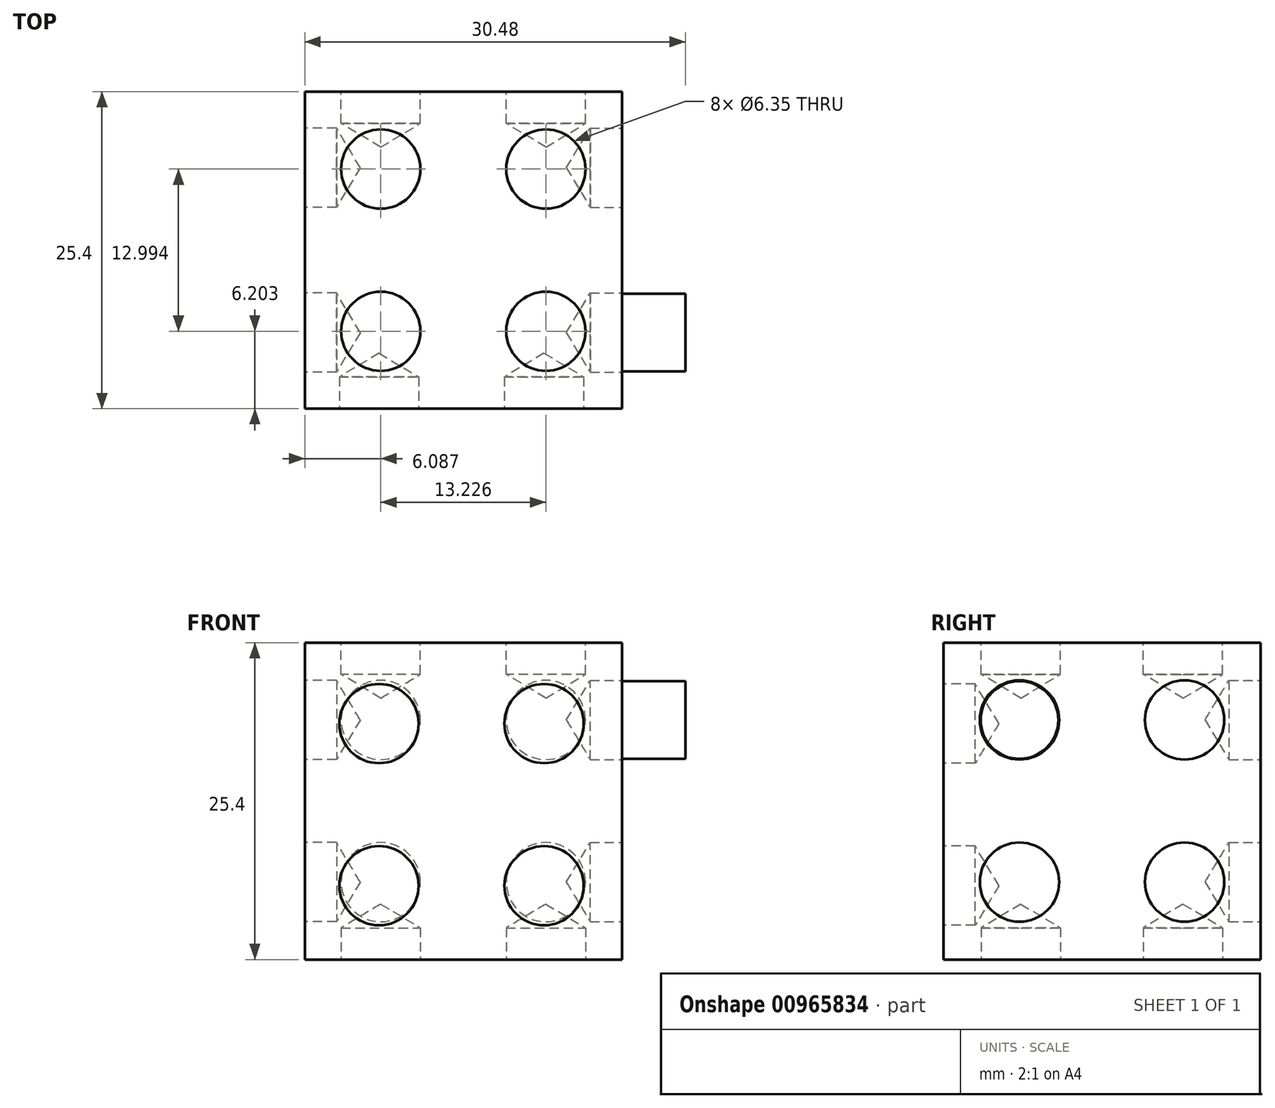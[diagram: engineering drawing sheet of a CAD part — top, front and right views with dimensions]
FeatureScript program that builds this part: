
annotation { "Feature Type Name" : "Feature", "Feature Type Description" : "" }
export const myFeature = defineFeature(function(context is Context, id is Id, definition is map)
    precondition{}
    {
        {
            var Q0;
            Q0=qCreatedBy(makeId("Front.planeOp"),FACE);
            var sketch = newSketch(context, id + "F0", { "sketchPlane" : qUnion([Q0])});
            skLineSegment(sketch, "E0.bottom", {"start": v(12.7, -12.7) * mm, "end": v(-12.7, -12.7) * mm});
            skLineSegment(sketch, "E0.top", {"start": v(12.7, 12.7) * mm, "end": v(-12.7, 12.7) * mm});
            skLineSegment(sketch, "E0.left", {"start": v(12.7, -12.7) * mm, "end": v(12.7, 12.7) * mm});
            skLineSegment(sketch, "E0.right", {"start": v(-12.7, -12.7) * mm, "end": v(-12.7, 12.7) * mm});
            skPoint(sketch, "E0.middle", {"position": v(0, 0) * mm});
            skSolve(sketch);
        }
        {
            var Q0;
            Q0 = qSketchRegion(id + "F0", true);
            extrude(context, id + "F1", {"entities" : qUnion([Q0]), "endBound" : BoundingType.SYMMETRIC, "depth" : 25.4 * mm, "offsetDistance" : 25.4 * mm});
        }
        {
            var Q0;
            Q0=makeQuery(id+"F1.opExtrude","CAP_FACE",FACE,{"disambiguationData":[OSD([sQuery(id+"F0.wireOp",EDGE,"E0.bottom"),sQuery(id+"F0.wireOp",EDGE,"E0.top"),sQuery(id+"F0.wireOp",EDGE,"E0.left"),sQuery(id+"F0.wireOp",EDGE,"E0.right")])],"isStart":false});
            var sketch = newSketch(context, id + "F2", { "sketchPlane" : qUnion([Q0])});
            skPoint(sketch, "E1", {"position": v(-6.76, 6.21) * mm});
            skPoint(sketch, "E2", {"position": v(6.47, 6.21) * mm});
            skPoint(sketch, "E3", {"position": v(6.47, -6.78) * mm});
            skPoint(sketch, "E4", {"position": v(-6.76, -6.78) * mm});
            skSolve(sketch);
        }
        {
            var Q0;
            Q0=sQuery(id+"F2.wireOp",VERTEX,"E1");
            var Q1;
            Q1=sQuery(id+"F2.wireOp",VERTEX,"E2");
            var Q2;
            Q2=sQuery(id+"F2.wireOp",VERTEX,"E3");
            var Q3;
            Q3=sQuery(id+"F2.wireOp",VERTEX,"E4");
            var Q4;
            Q4=makeQuery(id+"F1.opExtrude","SWEPT_BODY",BODY,{"disambiguationData":[OSD([sQuery(id+"F0.wireOp",EDGE,"E0.bottom"),sQuery(id+"F0.wireOp",EDGE,"E0.top"),sQuery(id+"F0.wireOp",EDGE,"E0.left"),sQuery(id+"F0.wireOp",EDGE,"E0.right")])]});
            hole(context, id + "F3", {"style" : HoleStyle.SIMPLE, "endStyle" : HoleEndStyle.BLIND, "holeDiameter" : 6.35 * mm, "majorDiameter" : 6 * mm, "holeDepth" : 2.54 * mm, "isTappedThrough" : true, "tappedDepth" : 12.7 * mm, "tapClearance" : 3, "startFromSketch" : true, "locations" : qUnion([Q0, Q1, Q2, Q3]), "scope" : qUnion([Q4])});
        }
        {
            var Q0;
            Q0=makeQuery(id+"F1.opExtrude","SWEPT_FACE",FACE,{"disambiguationData":[OSD([sQuery(id+"F0.wireOp",EDGE,"E0.left")])]});
            var sketch = newSketch(context, id + "F4", { "sketchPlane" : qUnion([Q0])});
            skPoint(sketch, "E5", {"position": v(-6.61, 6.5) * mm});
            skPoint(sketch, "E6", {"position": v(6.61, 6.5) * mm});
            skPoint(sketch, "E7", {"position": v(6.61, -6.5) * mm});
            skPoint(sketch, "E8", {"position": v(-6.61, -6.5) * mm});
            skSolve(sketch);
        }
        {
            var Q0;
            Q0=sQuery(id+"F4.wireOp",VERTEX,"E5");
            var Q1;
            Q1=sQuery(id+"F4.wireOp",VERTEX,"E6");
            var Q2;
            Q2=sQuery(id+"F4.wireOp",VERTEX,"E7");
            var Q3;
            Q3=sQuery(id+"F4.wireOp",VERTEX,"E8");
            var Q4;
            Q4=makeQuery(id+"F1.opExtrude","SWEPT_BODY",BODY,{"disambiguationData":[OSD([sQuery(id+"F0.wireOp",EDGE,"E0.bottom"),sQuery(id+"F0.wireOp",EDGE,"E0.top"),sQuery(id+"F0.wireOp",EDGE,"E0.left"),sQuery(id+"F0.wireOp",EDGE,"E0.right")])]});
            hole(context, id + "F5", {"style" : HoleStyle.SIMPLE, "endStyle" : HoleEndStyle.BLIND, "holeDiameter" : 6.35 * mm, "majorDiameter" : 6.35 * mm, "holeDepth" : 2.54 * mm, "isTappedThrough" : true, "tappedDepth" : 12.7 * mm, "tapClearance" : 3, "startFromSketch" : true, "locations" : qUnion([Q0, Q1, Q2, Q3]), "scope" : qUnion([Q4])});
        }
        {
            var Q0;
            Q0=makeQuery(id+"F1.opExtrude","CAP_FACE",FACE,{"disambiguationData":[OSD([sQuery(id+"F0.wireOp",EDGE,"E0.bottom"),sQuery(id+"F0.wireOp",EDGE,"E0.top"),sQuery(id+"F0.wireOp",EDGE,"E0.left"),sQuery(id+"F0.wireOp",EDGE,"E0.right")])],"isStart":true});
            var sketch = newSketch(context, id + "F6", { "sketchPlane" : qUnion([Q0])});
            skPoint(sketch, "E9", {"position": v(-6.61, 6.5) * mm});
            skPoint(sketch, "E10", {"position": v(6.61, 6.5) * mm});
            skPoint(sketch, "E11", {"position": v(6.61, -6.5) * mm});
            skPoint(sketch, "E12", {"position": v(-6.61, -6.5) * mm});
            skSolve(sketch);
        }
        {
            var Q0;
            Q0=sQuery(id+"F6.wireOp",VERTEX,"E9");
            var Q1;
            Q1=sQuery(id+"F6.wireOp",VERTEX,"E10");
            var Q2;
            Q2=sQuery(id+"F6.wireOp",VERTEX,"E11");
            var Q3;
            Q3=sQuery(id+"F6.wireOp",VERTEX,"E12");
            var Q4;
            Q4=makeQuery(id+"F1.opExtrude","SWEPT_BODY",BODY,{"disambiguationData":[OSD([sQuery(id+"F0.wireOp",EDGE,"E0.bottom"),sQuery(id+"F0.wireOp",EDGE,"E0.top"),sQuery(id+"F0.wireOp",EDGE,"E0.left"),sQuery(id+"F0.wireOp",EDGE,"E0.right")])]});
            hole(context, id + "F7", {"style" : HoleStyle.SIMPLE, "endStyle" : HoleEndStyle.BLIND, "holeDiameter" : 6.35 * mm, "majorDiameter" : 6.35 * mm, "holeDepth" : 2.54 * mm, "isTappedThrough" : true, "tappedDepth" : 12.7 * mm, "tapClearance" : 3, "startFromSketch" : true, "locations" : qUnion([Q0, Q1, Q2, Q3]), "scope" : qUnion([Q4])});
        }
        {
            var Q0;
            Q0=makeQuery(id+"F1.opExtrude","SWEPT_FACE",FACE,{"disambiguationData":[OSD([sQuery(id+"F0.wireOp",EDGE,"E0.right")])]});
            var sketch = newSketch(context, id + "F8", { "sketchPlane" : qUnion([Q0])});
            skPoint(sketch, "E13", {"position": v(-6.61, 6.5) * mm});
            skPoint(sketch, "E14", {"position": v(6.61, 6.5) * mm});
            skPoint(sketch, "E15", {"position": v(6.61, -6.5) * mm});
            skPoint(sketch, "E16", {"position": v(-6.61, -6.5) * mm});
            skSolve(sketch);
        }
        {
            var Q0;
            Q0=sQuery(id+"F8.wireOp",VERTEX,"E13");
            var Q1;
            Q1=sQuery(id+"F8.wireOp",VERTEX,"E14");
            var Q2;
            Q2=sQuery(id+"F8.wireOp",VERTEX,"E15");
            var Q3;
            Q3=sQuery(id+"F8.wireOp",VERTEX,"E16");
            var Q4;
            Q4=makeQuery(id+"F1.opExtrude","SWEPT_BODY",BODY,{"disambiguationData":[OSD([sQuery(id+"F0.wireOp",EDGE,"E0.bottom"),sQuery(id+"F0.wireOp",EDGE,"E0.top"),sQuery(id+"F0.wireOp",EDGE,"E0.left"),sQuery(id+"F0.wireOp",EDGE,"E0.right")])]});
            hole(context, id + "F9", {"style" : HoleStyle.SIMPLE, "endStyle" : HoleEndStyle.BLIND, "holeDiameter" : 6.35 * mm, "majorDiameter" : 6.35 * mm, "holeDepth" : 2.54 * mm, "isTappedThrough" : true, "tappedDepth" : 12.7 * mm, "tapClearance" : 3, "startFromSketch" : true, "locations" : qUnion([Q0, Q1, Q2, Q3]), "scope" : qUnion([Q4])});
        }
        {
            var Q0;
            Q0=makeQuery(id+"F1.opExtrude","SWEPT_FACE",FACE,{"disambiguationData":[OSD([sQuery(id+"F0.wireOp",EDGE,"E0.top")])]});
            var sketch = newSketch(context, id + "F10", { "sketchPlane" : qUnion([Q0])});
            skPoint(sketch, "E17", {"position": v(-6.61, 6.5) * mm});
            skPoint(sketch, "E18", {"position": v(6.61, 6.5) * mm});
            skPoint(sketch, "E19", {"position": v(6.61, -6.5) * mm});
            skPoint(sketch, "E20", {"position": v(-6.61, -6.5) * mm});
            skSolve(sketch);
        }
        {
            var Q0;
            Q0=sQuery(id+"F10.wireOp",VERTEX,"E17");
            var Q1;
            Q1=sQuery(id+"F10.wireOp",VERTEX,"E18");
            var Q2;
            Q2=sQuery(id+"F10.wireOp",VERTEX,"E19");
            var Q3;
            Q3=sQuery(id+"F10.wireOp",VERTEX,"E20");
            var Q4;
            Q4=makeQuery(id+"F1.opExtrude","SWEPT_BODY",BODY,{"disambiguationData":[OSD([sQuery(id+"F0.wireOp",EDGE,"E0.bottom"),sQuery(id+"F0.wireOp",EDGE,"E0.top"),sQuery(id+"F0.wireOp",EDGE,"E0.left"),sQuery(id+"F0.wireOp",EDGE,"E0.right")])]});
            hole(context, id + "F11", {"style" : HoleStyle.SIMPLE, "endStyle" : HoleEndStyle.BLIND, "holeDiameter" : 6.35 * mm, "majorDiameter" : 6.35 * mm, "holeDepth" : 2.54 * mm, "isTappedThrough" : true, "tappedDepth" : 12.7 * mm, "tapClearance" : 3, "startFromSketch" : true, "locations" : qUnion([Q0, Q1, Q2, Q3]), "scope" : qUnion([Q4])});
        }
        {
            var Q0;
            Q0=makeQuery(id+"F1.opExtrude","SWEPT_FACE",FACE,{"disambiguationData":[OSD([sQuery(id+"F0.wireOp",EDGE,"E0.bottom")])]});
            var sketch = newSketch(context, id + "F12", { "sketchPlane" : qUnion([Q0])});
            skPoint(sketch, "E21", {"position": v(-6.61, 6.5) * mm});
            skPoint(sketch, "E22", {"position": v(6.61, 6.5) * mm});
            skPoint(sketch, "E23", {"position": v(6.61, -6.5) * mm});
            skPoint(sketch, "E24", {"position": v(-6.61, -6.5) * mm});
            skSolve(sketch);
        }
        {
            var Q0;
            Q0=sQuery(id+"F12.wireOp",VERTEX,"E21");
            var Q1;
            Q1=sQuery(id+"F12.wireOp",VERTEX,"E22");
            var Q2;
            Q2=sQuery(id+"F12.wireOp",VERTEX,"E23");
            var Q3;
            Q3=sQuery(id+"F12.wireOp",VERTEX,"E24");
            var Q4;
            Q4=makeQuery(id+"F1.opExtrude","SWEPT_BODY",BODY,{"disambiguationData":[OSD([sQuery(id+"F0.wireOp",EDGE,"E0.bottom"),sQuery(id+"F0.wireOp",EDGE,"E0.top"),sQuery(id+"F0.wireOp",EDGE,"E0.left"),sQuery(id+"F0.wireOp",EDGE,"E0.right")])]});
            hole(context, id + "F13", {"style" : HoleStyle.SIMPLE, "endStyle" : HoleEndStyle.BLIND, "holeDiameter" : 6.35 * mm, "majorDiameter" : 6.35 * mm, "holeDepth" : 2.54 * mm, "isTappedThrough" : true, "tappedDepth" : 12.7 * mm, "tapClearance" : 3, "startFromSketch" : true, "locations" : qUnion([Q0, Q1, Q2, Q3]), "scope" : qUnion([Q4])});
        }
        {
            var Q0;
            Q0=makeQuery(id+"F1.opExtrude","SWEPT_FACE",FACE,{"disambiguationData":[OSD([sQuery(id+"F0.wireOp",EDGE,"E0.left")])]});
            var sketch = newSketch(context, id + "F14", { "sketchPlane" : qUnion([Q0])});
            skPoint(sketch, "E25", {"position": v(-6.61, 6.5) * mm});
            skCircle(sketch, "E26", {"center": v(-6.61, 6.5) * mm, "radius": 3.11 * mm});
            skSolve(sketch);
        }
        {
            var Q0;
            Q0 = qSketchRegion(id + "F14", true);
            extrude(context, id + "F15", {"entities" : qUnion([Q0]), "depth" : 5.08 * mm, "offsetDistance" : 25.4 * mm});
        }
    });
